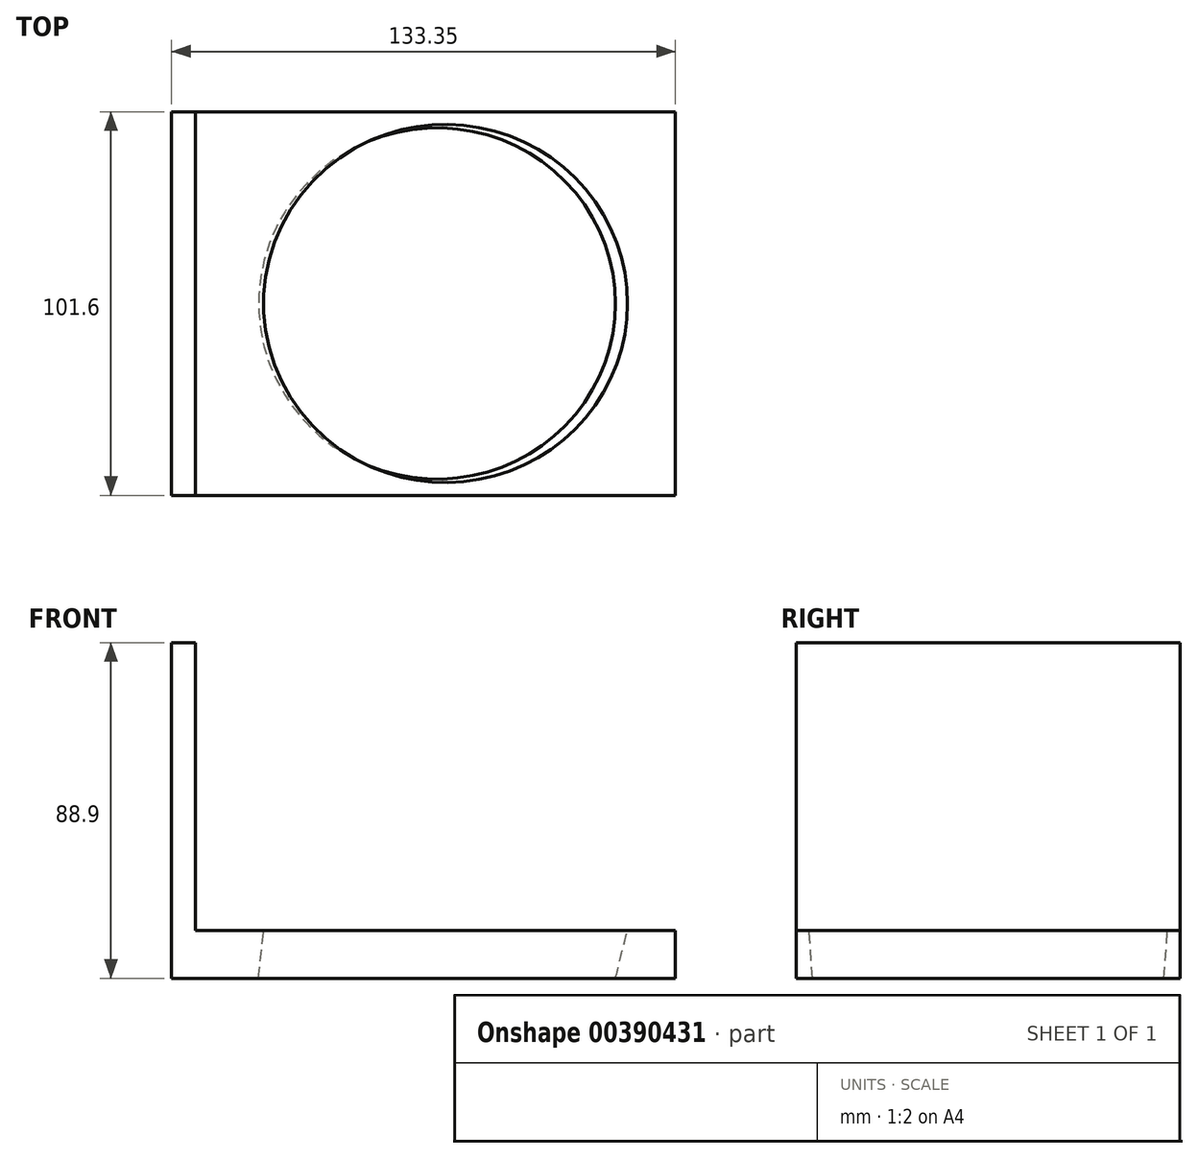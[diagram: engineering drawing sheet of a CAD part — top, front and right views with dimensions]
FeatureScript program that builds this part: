
annotation { "Feature Type Name" : "Feature", "Feature Type Description" : "" }
export const myFeature = defineFeature(function(context is Context, id is Id, definition is map)
    precondition{}
    {
        {
            var Q0;
            Q0=qCreatedBy(makeId("Front.planeOp"),FACE);
            var sketch = newSketch(context, id + "F0", { "sketchPlane" : qUnion([Q0])});
            skLineSegment(sketch, "E0.top", {"start": v(0, 88.9) * mm, "end": v(6.35, 88.9) * mm});
            skLineSegment(sketch, "E0.left", {"start": v(0, 0) * mm, "end": v(0, 88.9) * mm});
            skLineSegment(sketch, "E0.right", {"start": v(6.35, 12.7) * mm, "end": v(6.35, 88.9) * mm});
            skLineSegment(sketch, "E1.bottom", {"start": v(0, 0) * mm, "end": v(133.35, 0) * mm});
            skLineSegment(sketch, "E1.top", {"start": v(6.35, 12.7) * mm, "end": v(133.35, 12.7) * mm});
            skLineSegment(sketch, "E1.right", {"start": v(133.35, 0) * mm, "end": v(133.35, 12.7) * mm});
            skSolve(sketch);
        }
        {
            var Q0;
            Q0 = qSketchRegion(id + "F0", true);
            extrude(context, id + "F1", {"entities" : qUnion([Q0]), "depth" : 101.6 * mm, "symmetric" : true});
        }
        {
            var Q0;
            Q0=qCreatedBy(makeId("Front.planeOp"),FACE);
            var sketch = newSketch(context, id + "F2", { "sketchPlane" : qUnion([Q0])});
            skLineSegment(sketch, "E2", {"start": v(64.56, -29) * mm, "end": v(73.38, 21.04) * mm});
            skLineSegment(sketch, "E3", {"start": v(64.56, -29) * mm, "end": v(108.33, -36.71) * mm});
            skLineSegment(sketch, "E4", {"start": v(108.33, -36.71) * mm, "end": v(120.65, 12.7) * mm});
            skLineSegment(sketch, "E5", {"start": v(120.65, 12.7) * mm, "end": v(73.38, 21.04) * mm});
            skSolve(sketch);
        }
        {
            var Q0;
            Q0 = qSketchRegion(id + "F2", true);
            var Q1;
            Q1=sQuery(id+"F2.wireOp",EDGE,"E2");
            revolve(context, id + "F3", {"operationType" : NewBodyOperationType.REMOVE, "surfaceOperationType" : NewSurfaceOperationType.NEW, "entities" : qUnion([Q0]), "axis" : qUnion([Q1]), "revolveType" : RevolveType.FULL, "oppositeDirection" : true});
        }
    });
